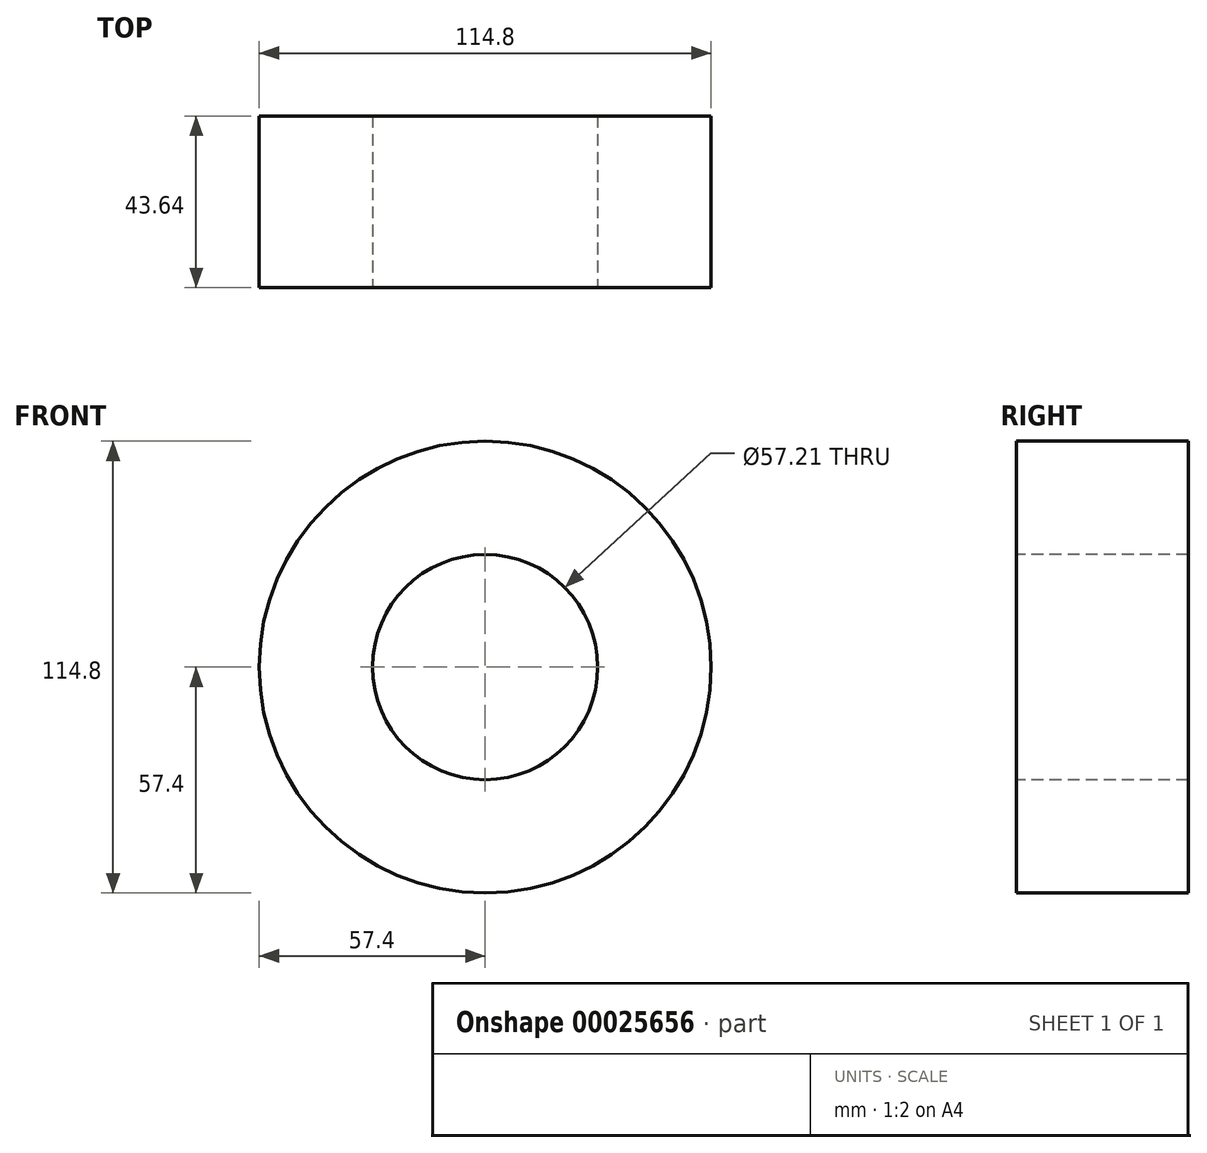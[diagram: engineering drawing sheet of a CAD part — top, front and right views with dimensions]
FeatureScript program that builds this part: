
annotation { "Feature Type Name" : "Feature", "Feature Type Description" : "" }
export const myFeature = defineFeature(function(context is Context, id is Id, definition is map)
    precondition{}
    {
        {
            var Q0;
            Q0=qCreatedBy(makeId("Front.planeOp"),FACE);
            var sketch = newSketch(context, id + "F0", { "sketchPlane" : qUnion([Q0])});
            skCircle(sketch, "E0", {"center": v(0, 0) * mm, "radius": 57.4 * mm});
            skSolve(sketch);
        }
        {
            var Q0;
            Q0=makeQuery(id+"F0.imprint","IMPRINT",FACE,{"disambiguationData":[TD([[makeQuery(id+"F0.imprint","IMPRINT",EDGE,{"derivedFrom":sQuery(id+"F0.wireOp",EDGE,"E0")}),1.0]])]});
            var sketch = newSketch(context, id + "F6", { "sketchPlane" : qUnion([Q0])});
            skSolve(sketch);
        }
        {
            var Q0;
            Q0=makeQuery(id+"F6.imprint","IMPRINT",FACE,{"disambiguationData":[TD([[makeQuery(id+"F6.imprint","IMPRINT",EDGE,{"derivedFrom":makeQuery(id+"F0.imprint","IMPRINT",EDGE,{"derivedFrom":sQuery(id+"F0.wireOp",EDGE,"E0")})}),1.0]])]});
            extrude(context, id + "F7", {"entities" : qUnion([Q0]), "depth" : 25.4 * mm});
        }
        {
            var Q0;
            Q0=makeQuery(id+"F7.opExtrude","CAP_FACE",FACE,{"disambiguationData":[OSD([sQuery(id+"F0.wireOp",EDGE,"E0")])],"isStart":false});
            extrude(context, id + "F8", {"entities" : qUnion([Q0]), "operationType" : NewBodyOperationType.ADD, "depth" : 18.24 * mm});
        }
        {
            var Q0;
            Q0=makeQuery(id+"F8.opExtrude","CAP_FACE",FACE,{"disambiguationData":[OSD([sQuery(id+"F0.wireOp",EDGE,"E0")])],"isStart":false});
            var sketch = newSketch(context, id + "F1", { "sketchPlane" : qUnion([Q0])});
            skCircle(sketch, "E1", {"center": v(0, 0) * mm, "radius": 28.6 * mm});
            skSolve(sketch);
        }
        {
            var Q0;
            Q0=sQuery(id+"F1.wireOp",VERTEX,"E1.center");
            var Q1;
            Q1=makeQuery(id+"F7.opExtrude","SWEPT_BODY",BODY,{"disambiguationData":[OSD([sQuery(id+"F0.wireOp",EDGE,"E0")])]});
            hole(context, id + "F9", {"style" : HoleStyle.SIMPLE, "holeDiameter" : 25.4 * mm, "endStyle" : HoleEndStyle.THROUGH, "locations" : qUnion([Q0]), "scope" : qUnion([Q1])});
        }
        {
            var Q0;
            Q0 = qSketchRegion(id + "F1", true);
            extrude(context, id + "F2", {"entities" : qUnion([Q0]), "operationType" : NewBodyOperationType.REMOVE, "depth" : 64.5 * mm});
        }
        {
            var Q0;
            Q0 = qSketchRegion(id + "F1", true);
            extrude(context, id + "F3", {"entities" : qUnion([Q0]), "operationType" : NewBodyOperationType.REMOVE, "oppositeDirection" : true, "depth" : 76.7 * mm});
        }
    });
